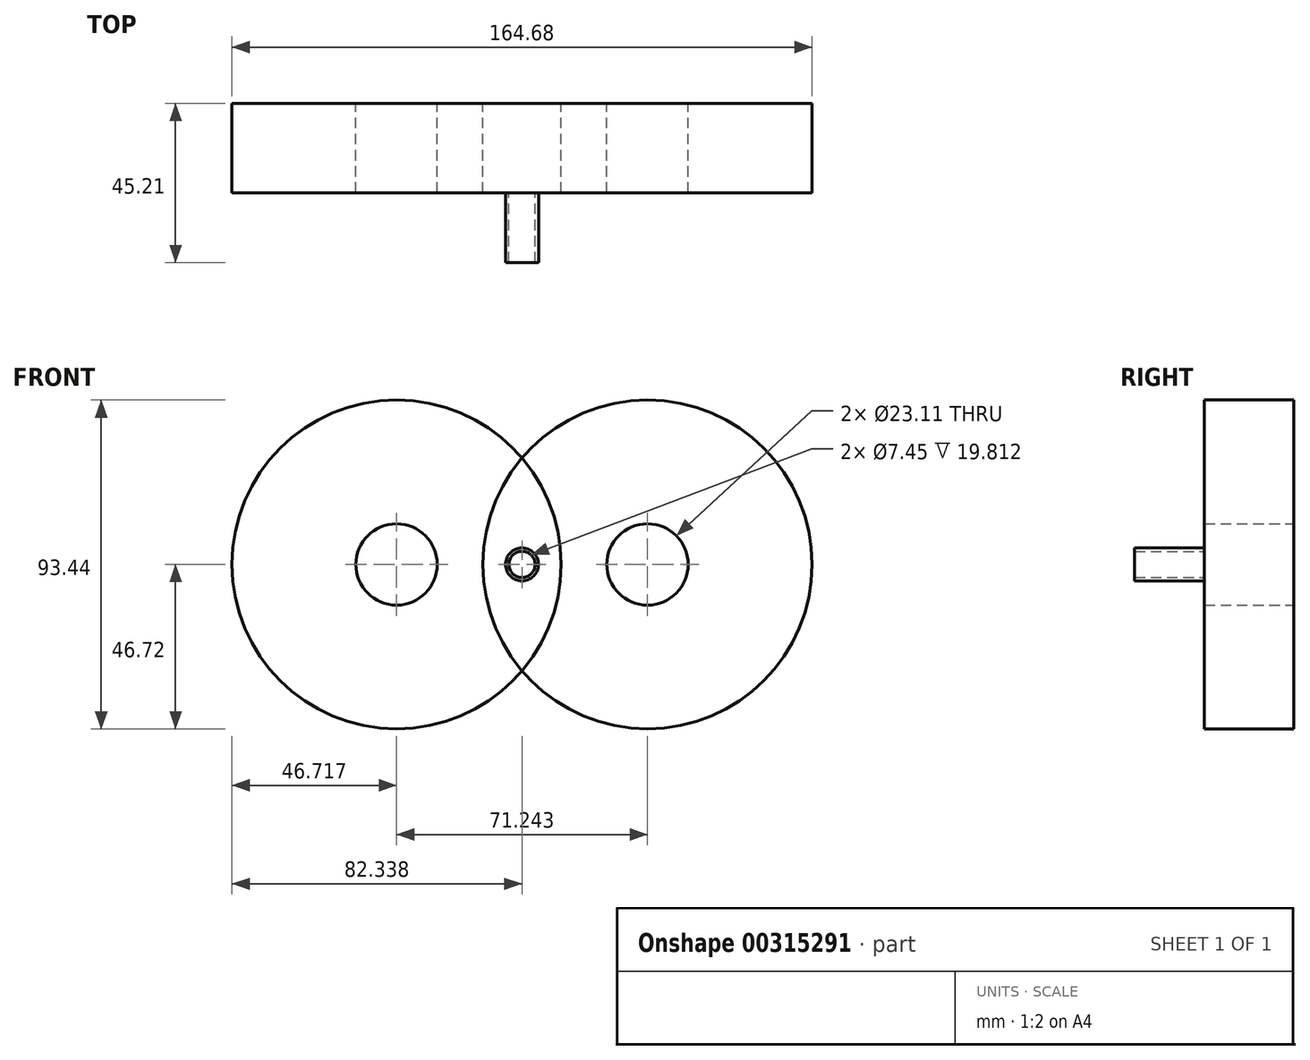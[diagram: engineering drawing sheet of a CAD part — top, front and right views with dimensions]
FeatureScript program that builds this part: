
annotation { "Feature Type Name" : "Feature", "Feature Type Description" : "" }
export const myFeature = defineFeature(function(context is Context, id is Id, definition is map)
    precondition{}
    {
        {
            var Q0;
            Q0=qCreatedBy(makeId("Front.planeOp"),FACE);
            var sketch = newSketch(context, id + "F0", { "sketchPlane" : qUnion([Q0])});
            skCircle(sketch, "E0", {"center": v(0, 0) * mm, "radius": 46.72 * mm});
            skCircle(sketch, "E1", {"center": v(0, 0) * mm, "radius": 7.88 * mm});
            skCircle(sketch, "E2", {"center": v(0, 0) * mm, "radius": 11.55 * mm});
            skSolve(sketch);
        }
        {
            var Q0;
            Q0 = qSketchRegion(id + "F0", true);
            extrude(context, id + "F1", {"entities" : qUnion([Q0]), "depth" : 25.4 * mm});
        }
        {
            var Q0;
            Q0=makeQuery(id+"F1.opExtrude","CAP_FACE",FACE,{"disambiguationData":[OSD([sQuery(id+"F0.wireOp",EDGE,"E0"),sQuery(id+"F0.wireOp",EDGE,"E2")])],"isStart":false});
            var sketch = newSketch(context, id + "F2", { "sketchPlane" : qUnion([Q0])});
            skCircle(sketch, "E3", {"center": v(-35.62, 0) * mm, "radius": 3.73 * mm});
            skCircle(sketch, "E4", {"center": v(-35.62, 0) * mm, "radius": 4.67 * mm});
            skSolve(sketch);
        }
        {
            var Q0;
            Q0 = qSketchRegion(id + "F2", true);
            extrude(context, id + "F3", {"entities" : qUnion([Q0]), "operationType" : NewBodyOperationType.ADD, "depth" : 19.8 * mm});
        }
        {
            var Q0;
            Q0=makeQuery(id+"F1.opExtrude","SWEPT_BODY",BODY,{"disambiguationData":[OSD([sQuery(id+"F0.wireOp",EDGE,"E0"),sQuery(id+"F0.wireOp",EDGE,"E2")])]});
            var Q1;
            Q1=makeQuery(id+"F3.opExtrude","SWEPT_FACE",FACE,{"disambiguationData":[OSD([sQuery(id+"F2.wireOp",EDGE,"E4")])]});
            circularPattern(context, id + "F4", {"entities" : qUnion([Q0]), "axis" : qUnion([Q1]), "angle" : 360 * degree, "instanceCount" : 2, "equalSpace" : true});
        }
    });
